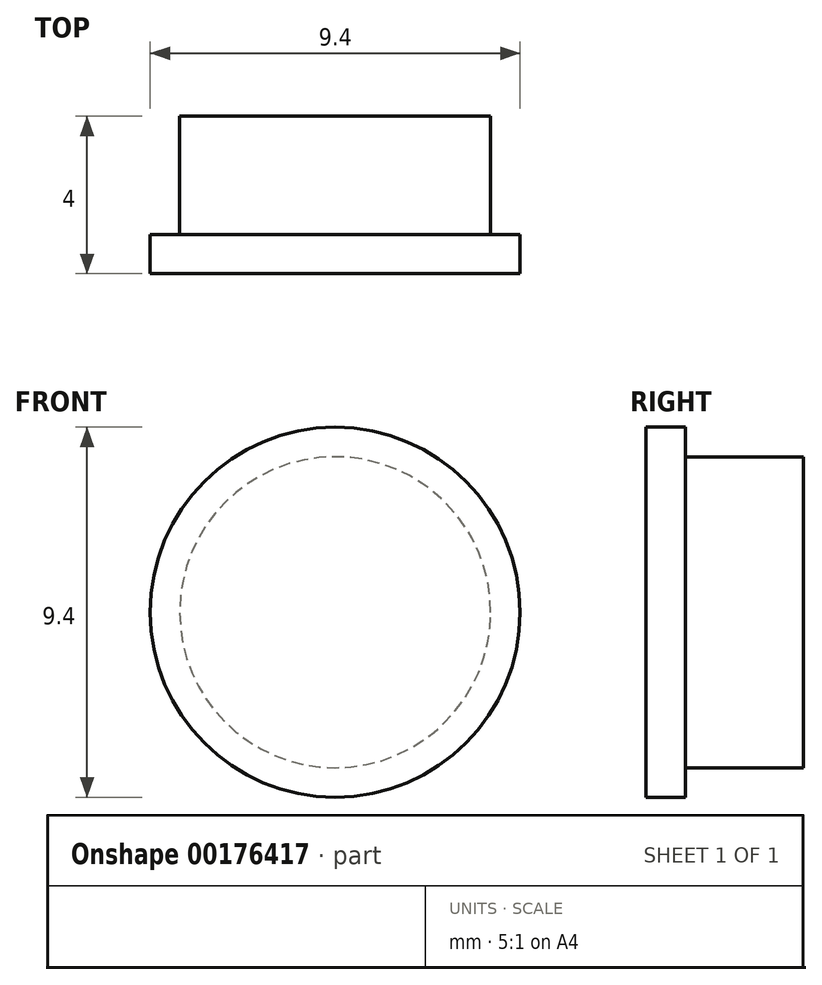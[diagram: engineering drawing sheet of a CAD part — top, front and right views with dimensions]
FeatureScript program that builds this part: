
annotation { "Feature Type Name" : "Feature", "Feature Type Description" : "" }
export const myFeature = defineFeature(function(context is Context, id is Id, definition is map)
    precondition{}
    {
        {
            var Q0;
            Q0=qCreatedBy(makeId("Right.planeOp"),FACE);
            var sketch = newSketch(context, id + "F0", { "sketchPlane" : qUnion([Q0])});
            skLineSegment(sketch, "E0", {"start": v(11.47, 0) * mm, "end": v(0, 0) * mm, "construction": true});
            skLineSegment(sketch, "E1", {"start": v(4, 0) * mm, "end": v(0, 0) * mm});
            skLineSegment(sketch, "E2", {"start": v(4, 0) * mm, "end": v(4, 3.95) * mm});
            skLineSegment(sketch, "E3", {"start": v(1, 3.95) * mm, "end": v(4, 3.95) * mm});
            skLineSegment(sketch, "E4", {"start": v(1, 3.95) * mm, "end": v(1, 4.7) * mm});
            skLineSegment(sketch, "E5", {"start": v(0, 4.7) * mm, "end": v(1, 4.7) * mm});
            skLineSegment(sketch, "E6", {"start": v(0, 4.7) * mm, "end": v(0, 0) * mm});
            skSolve(sketch);
        }
        {
            var Q0;
            Q0=makeQuery(id+"F0.imprint","IMPRINT",FACE,{"disambiguationData":[TD([[makeQuery(id+"F0.imprint","IMPRINT",EDGE,{"derivedFrom":sQuery(id+"F0.wireOp",EDGE,"E1")}),-1.0]])]});
            var Q1;
            Q1=sQuery(id+"F0.wireOp",EDGE,"E0");
            revolve(context, id + "F1", {"entities" : qUnion([Q0]), "axis" : qUnion([Q1]), "revolveType" : RevolveType.FULL});
        }
    });
